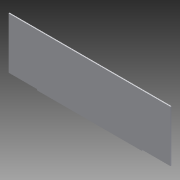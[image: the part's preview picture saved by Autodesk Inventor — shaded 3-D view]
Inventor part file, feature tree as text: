
AUTODESK INVENTOR PART (.ipt)
format: ipt  version: 2012 (Build 160160000, 160)  size: 75,264 bytes
history: native  units: in
note: dims shown in document units (in); Inventor stores cm internally (conversion verified against a paired STEP export)
features: extrude x1, sketch x1
ambient origin geometry x8: Origin, YZ Plane, XZ Plane, XY Plane, X Axis, Y Axis, Z Axis, Center Point
bodies: Solid1 (feature_tree)
feature tree (2):
  extrude  "Extrusion1"  Depth=37.0in
  sketch  "Sketch1"  dims[d0=12.0in d1=37.0in d2=6.5in d3=0.25in d4=0.25in d5=0.0in]
